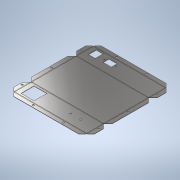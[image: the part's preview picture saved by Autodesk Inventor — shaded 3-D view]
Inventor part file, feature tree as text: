
AUTODESK INVENTOR PART (.ipt)
format: ipt  version: 2020.3 (Build 243373000, 373)  size: 355,840 bytes
history: native  units: mm
features: sheet_metal_op x8, sketch x8, other x4, hole x3, extrude x2
ambient origin geometry x8: Origin, YZ Plane, XZ Plane, XY Plane, X Axis, Y Axis, Z Axis, Center Point
bodies: Solid1 (feature_tree)
feature tree (25):
  sheet_metal_op  "Face1"
  sheet_metal_op  "Flange1"
  sheet_metal_op  "Flange2"
  other  "Corner Chamfer2"
  hole  "Hole1"  [1 undecoded]
  hole  "Hole2"  [1 undecoded]
  extrude  "Extrusion1"  Depth=2.0mm
  extrude  "Extrusion2"  Depth=1.0mm TaperAngle=90.0deg
  sheet_metal_op  "Unfold1"
  hole  "Hole4"  [1 undecoded]
  sketch  "Sketch1"  dims[d0=248.0mm d1=155.0mm]
  other  "Plate1"
  sketch  "Sketch2"  dims[d2=1.0mm d3=1.0mm]
  other  "Plate2"
  sheet_metal_op  "Bend1"
  sheet_metal_op  "Corner1"
  sketch  "Sketch3"  dims[d4=0.5mm d5=2.0mm]
  other  "Plate3"
  sheet_metal_op  "Bend2"
  sheet_metal_op  "Corner2"
  sketch  "Sketch6"  dims[d6=1.0mm d7=60.0mm d8=90.0deg d9=1.0mm]
  sketch  "Sketch7"  dims[d10=4.0mm d11=1.0mm]
  sketch  "Sketch8"  dims[d12=1.0mm]
  sketch  "Sketch10"  dims[d13=1.0mm]
  sketch  "Sketch11"  dims[d14=0.5mm d15=2.0mm d16=1.0mm d17=15.0mm d18=90.0deg d19=1.0mm d20=4.0mm d21=1.0mm d22=1.0mm d26=12.0mm d27=6.0mm d28=45.0deg d53=8.0mm d54=72.0mm d55=72.0mm d56=8.0mm d57=6.0mm d58=6.0mm d59=4.0mm d60=2.0mm d61=90.0deg d62=1.0mm d63=20.594885mm d64=8.0mm d65=8.0mm d66=8.0mm d67=77.5mm d68=25.0mm d69=6.0mm d70=6.0mm d71=4.0mm d72=2.0mm d73=90.0deg d74=1.0mm d75=20.594885mm d76=44.3mm d77=44.3mm d78=15.0mm d79=5.85mm d80=5.85mm d81=10.0mm d82=0.0mm d93=23.0mm d94=27.0mm d95=15.0mm d96=5.0mm d97=28.0mm d98=20.0mm d99=10.0mm d100=25.0mm d101=4.0mm d102=10.0mm d103=6.1mm d104=4.0mm d105=40.2mm d106=10.0mm d107=0.0mm d108=30.0mm d109=50.0mm d110=34.0mm d111=6.0mm d112=6.0mm d113=4.0mm d114=2.0mm d115=90.0deg d116=1.0mm d117=20.594885mm]
note: 3 required parameter values undecoded (feature->parameter linkage not recoverable at this tier; creation-order binding heuristic only, values carry confidence <= 0.55)
